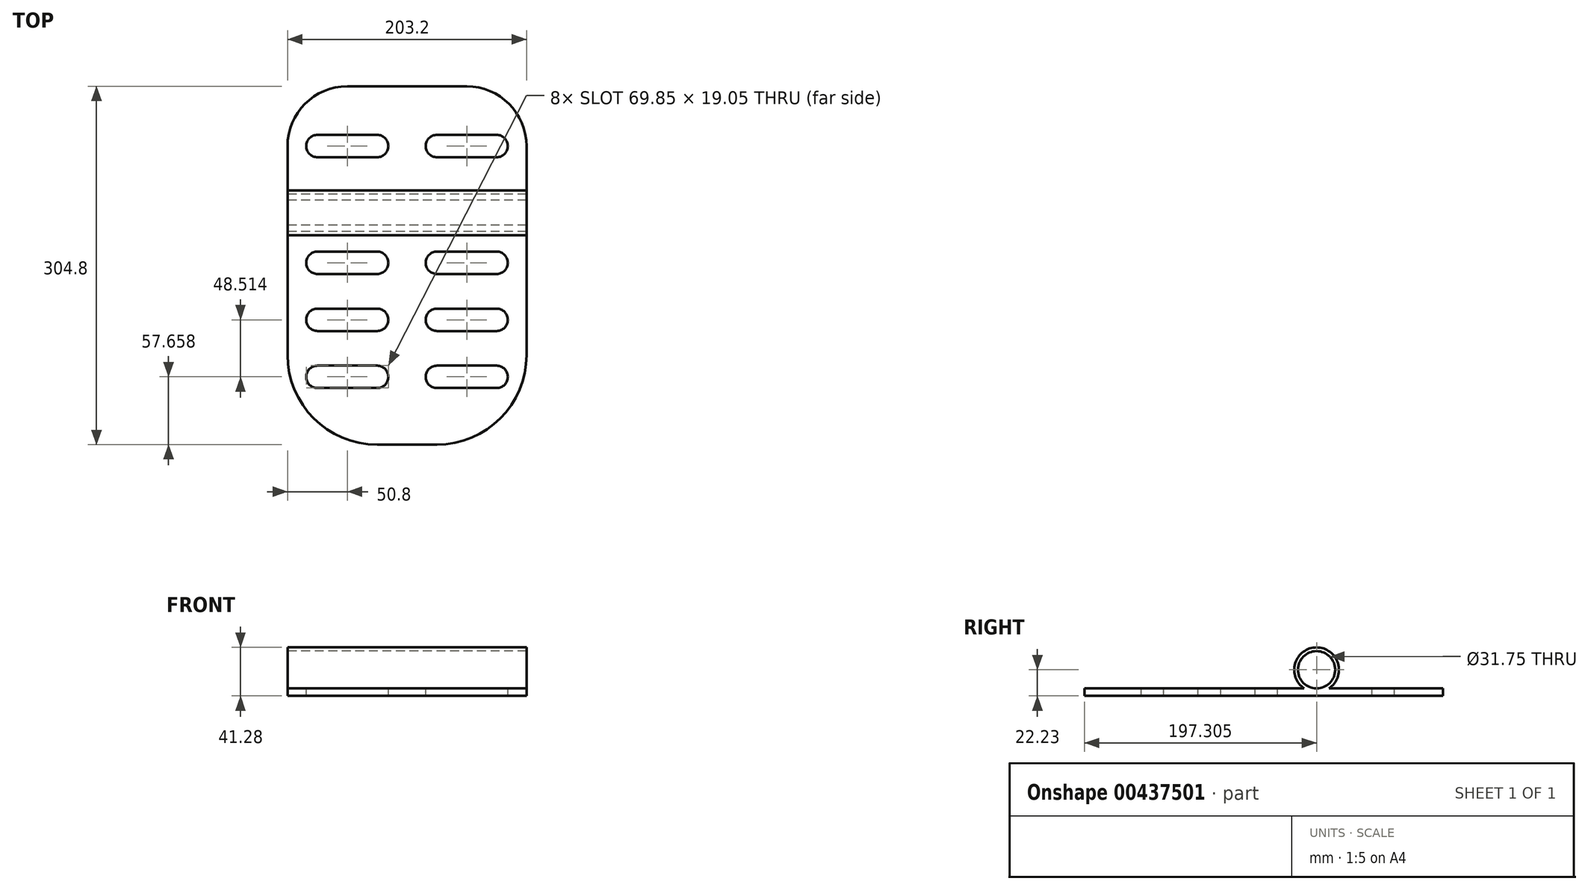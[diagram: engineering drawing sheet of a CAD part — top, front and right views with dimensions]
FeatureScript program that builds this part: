
annotation { "Feature Type Name" : "Feature", "Feature Type Description" : "" }
export const myFeature = defineFeature(function(context is Context, id is Id, definition is map)
    precondition{}
    {
        {
            var Q0;
            Q0=qCreatedBy(makeId("Right.planeOp"),FACE);
            var sketch = newSketch(context, id + "F0", { "sketchPlane" : qUnion([Q0])});
            skLineSegment(sketch, "E0", {"start": v(0, -15.88) * mm, "end": v(-254, -15.88) * mm});
            skLineSegment(sketch, "E1", {"start": v(-254, -15.88) * mm, "end": v(-254, -22.23) * mm});
            skLineSegment(sketch, "E2", {"start": v(-254, -22.23) * mm, "end": v(50.8, -22.23) * mm});
            skLineSegment(sketch, "E3", {"start": v(50.8, -22.23) * mm, "end": v(50.8, -15.87) * mm});
            skLineSegment(sketch, "E4", {"start": v(50.8, -15.87) * mm, "end": v(0, -15.88) * mm});
            skCircle(sketch, "E5", {"center": v(-56.7, 0) * mm, "radius": 15.88 * mm});
            skCircle(sketch, "E6", {"center": v(-56.7, 0) * mm, "radius": 19.05 * mm});
            skSolve(sketch);
        }
        {
            var Q0;
            Q0 = qSketchRegion(id + "F0", true);
            extrude(context, id + "F1", {"entities" : qUnion([Q0]), "depth" : 101.6 * mm, "offsetDistance" : 25.4 * mm, "hasSecondDirection" : true, "secondDirectionOppositeDirection" : true, "secondDirectionDepth" : 101.6 * mm});
        }
        {
            var Q0;
            Q0=makeQuery(id+"F1.opExtrude","SWEPT_FACE",FACE,{"disambiguationData":[OSD([sQuery(id+"F0.wireOp",EDGE,"E0")])]});
            var sketch = newSketch(context, id + "F2", { "sketchPlane" : qUnion([Q0])});
            skLineSegment(sketch, "E7", {"start": v(0, 0) * mm, "end": v(0, -254) * mm});
            skLineSegment(sketch, "E8", {"start": v(0, 0) * mm, "end": v(0, -19.05) * mm});
            skLineSegment(sketch, "E9", {"start": v(-101.6, -254) * mm, "end": v(-101.6, -177.8) * mm});
            skArc(sketch, "E10", {"start": v(-101.6, -177.8) * mm, "mid": v(-79.28, -231.68) * mm, "end": v(-25.4, -254) * mm});
            skArc(sketch, "E11.MirrorCS", {"start": v(101.6, -177.8) * mm, "mid": v(79.28, -231.68) * mm, "end": v(25.4, -254) * mm});
            skLineSegment(sketch, "E12.MirrorCS", {"start": v(101.6, -254) * mm, "end": v(101.6, -177.8) * mm});
            skLineSegment(sketch, "E13", {"start": v(-101.6, -254) * mm, "end": v(-25.4, -254) * mm});
            skLineSegment(sketch, "E14", {"start": v(25.4, -254) * mm, "end": v(101.6, -254) * mm});
            skSolve(sketch);
        }
        {
            var Q0;
            Q0 = qSketchRegion(id + "F2", true);
            extrude(context, id + "F3", {"entities" : qUnion([Q0]), "operationType" : NewBodyOperationType.REMOVE, "oppositeDirection" : true, "depth" : 25.4 * mm, "offsetDistance" : 25.4 * mm});
        }
        {
            var Q0;
            Q0=makeQuery(id+"F1.opExtrude","SWEPT_FACE",FACE,{"disambiguationData":[OSD([sQuery(id+"F0.wireOp",EDGE,"E0")])]});
            var sketch = newSketch(context, id + "F4", { "sketchPlane" : qUnion([Q0])});
            skLineSegment(sketch, "E15", {"start": v(0, 0) * mm, "end": v(0, -254) * mm});
            skLineSegment(sketch, "E16.direction1", {"start": v(-125.05, -60.33) * mm, "end": v(-76.2, -60.33) * mm, "construction": true});
            skArc(sketch, "E17.0.1.0", {"start": v(25.4, -9.52) * mm, "mid": v(15.88, 0) * mm, "end": v(25.4, 9.53) * mm});
            skArc(sketch, "E17.0.1.1", {"start": v(-25.4, -9.53) * mm, "mid": v(-15.87, 0) * mm, "end": v(-25.4, 9.53) * mm});
            skLineSegment(sketch, "E17.0.1.2", {"start": v(76.2, 9.52) * mm, "end": v(25.4, 9.52) * mm});
            skLineSegment(sketch, "E17.0.1.4", {"start": v(25.4, -9.53) * mm, "end": v(76.2, -9.53) * mm});
            skLineSegment(sketch, "E17.0.1.5", {"start": v(125.05, -9.53) * mm, "end": v(76.2, -9.53) * mm, "construction": true});
            skArc(sketch, "E17.0.1.6", {"start": v(76.2, 9.53) * mm, "mid": v(85.73, 0) * mm, "end": v(76.2, -9.52) * mm});
            skLineSegment(sketch, "E17.0.1.7", {"start": v(-76.2, 9.52) * mm, "end": v(-25.4, 9.52) * mm});
            skLineSegment(sketch, "E17.0.1.8", {"start": v(-25.4, -9.53) * mm, "end": v(-76.2, -9.53) * mm});
            skArc(sketch, "E17.0.1.9", {"start": v(-76.2, 9.53) * mm, "mid": v(-85.73, 0) * mm, "end": v(-76.2, -9.52) * mm});
            skLineSegment(sketch, "E18.0.1.0", {"start": v(-76.2, -89.79) * mm, "end": v(-25.4, -89.79) * mm});
            skLineSegment(sketch, "E18.0.1.1", {"start": v(-25.4, -108.84) * mm, "end": v(-76.2, -108.84) * mm});
            skArc(sketch, "E18.0.1.2", {"start": v(-76.2, -89.79) * mm, "mid": v(-85.73, -99.31) * mm, "end": v(-76.2, -108.84) * mm});
            skArc(sketch, "E18.0.1.3", {"start": v(-25.4, -108.84) * mm, "mid": v(-15.87, -99.31) * mm, "end": v(-25.4, -89.79) * mm});
            skLineSegment(sketch, "E18.0.2.0", {"start": v(-76.2, -138.3) * mm, "end": v(-25.4, -138.3) * mm});
            skLineSegment(sketch, "E18.0.2.1", {"start": v(-25.4, -157.35) * mm, "end": v(-76.2, -157.35) * mm});
            skArc(sketch, "E18.0.2.2", {"start": v(-76.2, -138.3) * mm, "mid": v(-85.73, -147.83) * mm, "end": v(-76.2, -157.35) * mm});
            skArc(sketch, "E18.0.2.3", {"start": v(-25.4, -157.35) * mm, "mid": v(-15.87, -147.83) * mm, "end": v(-25.4, -138.3) * mm});
            skLineSegment(sketch, "E18.0.3.0", {"start": v(-76.2, -186.82) * mm, "end": v(-25.4, -186.82) * mm});
            skLineSegment(sketch, "E18.0.3.1", {"start": v(-25.4, -205.87) * mm, "end": v(-76.2, -205.87) * mm});
            skArc(sketch, "E18.0.3.2", {"start": v(-76.2, -186.82) * mm, "mid": v(-85.73, -196.34) * mm, "end": v(-76.2, -205.87) * mm});
            skArc(sketch, "E18.0.3.3", {"start": v(-25.4, -205.87) * mm, "mid": v(-15.87, -196.34) * mm, "end": v(-25.4, -186.82) * mm});
            skLineSegment(sketch, "E19", {"start": v(0, 0) * mm, "end": v(-25.4, 0) * mm});
            skLineSegment(sketch, "E20.MirrorCS", {"start": v(25.4, -205.87) * mm, "end": v(76.2, -205.87) * mm});
            skArc(sketch, "E21.MirrorCS", {"start": v(76.2, -186.82) * mm, "mid": v(85.73, -196.34) * mm, "end": v(76.2, -205.87) * mm});
            skArc(sketch, "E22.MirrorCS", {"start": v(25.4, -205.87) * mm, "mid": v(15.88, -196.34) * mm, "end": v(25.4, -186.82) * mm});
            skLineSegment(sketch, "E23.MirrorCS", {"start": v(76.2, -186.82) * mm, "end": v(25.4, -186.82) * mm});
            skLineSegment(sketch, "E24.MirrorCS", {"start": v(25.4, -157.35) * mm, "end": v(76.2, -157.35) * mm});
            skArc(sketch, "E25.MirrorCS", {"start": v(25.4, -157.35) * mm, "mid": v(15.88, -147.83) * mm, "end": v(25.4, -138.3) * mm});
            skLineSegment(sketch, "E26.MirrorCS", {"start": v(76.2, -138.3) * mm, "end": v(25.4, -138.3) * mm});
            skArc(sketch, "E27.MirrorCS", {"start": v(76.2, -138.3) * mm, "mid": v(85.73, -147.83) * mm, "end": v(76.2, -157.35) * mm});
            skLineSegment(sketch, "E28.MirrorCS", {"start": v(76.2, -89.79) * mm, "end": v(25.4, -89.79) * mm});
            skLineSegment(sketch, "E29.MirrorCS", {"start": v(25.4, -108.84) * mm, "end": v(76.2, -108.84) * mm});
            skArc(sketch, "E30.MirrorCS", {"start": v(76.2, -89.79) * mm, "mid": v(85.73, -99.31) * mm, "end": v(76.2, -108.84) * mm});
            skArc(sketch, "E31.MirrorCS", {"start": v(25.4, -108.84) * mm, "mid": v(15.88, -99.31) * mm, "end": v(25.4, -89.79) * mm});
            skSolve(sketch);
        }
        {
            var Q0;
            Q0 = qSketchRegion(id + "F4", true);
            extrude(context, id + "F5", {"entities" : qUnion([Q0]), "operationType" : NewBodyOperationType.REMOVE, "oppositeDirection" : true, "depth" : 25.4 * mm, "offsetDistance" : 25.4 * mm});
        }
        {
            var Q0;
            Q0=makeQuery(id+"F1.opExtrude","CAP_EDGE",EDGE,{"disambiguationData":[OSD([sQuery(id+"F0.wireOp",EDGE,"E3")])],"isStart":false});
            var Q1;
            Q1=makeQuery(id+"F1.opExtrude","CAP_EDGE",EDGE,{"disambiguationData":[OSD([sQuery(id+"F0.wireOp",EDGE,"E3")])],"isStart":true});
            fillet(context, id + "F6", {"entities" : qUnion([Q0, Q1]), "radius" : 50.8 * mm, "tangentPropagation" : true, "allowEdgeOverflow" : false});
        }
    });
